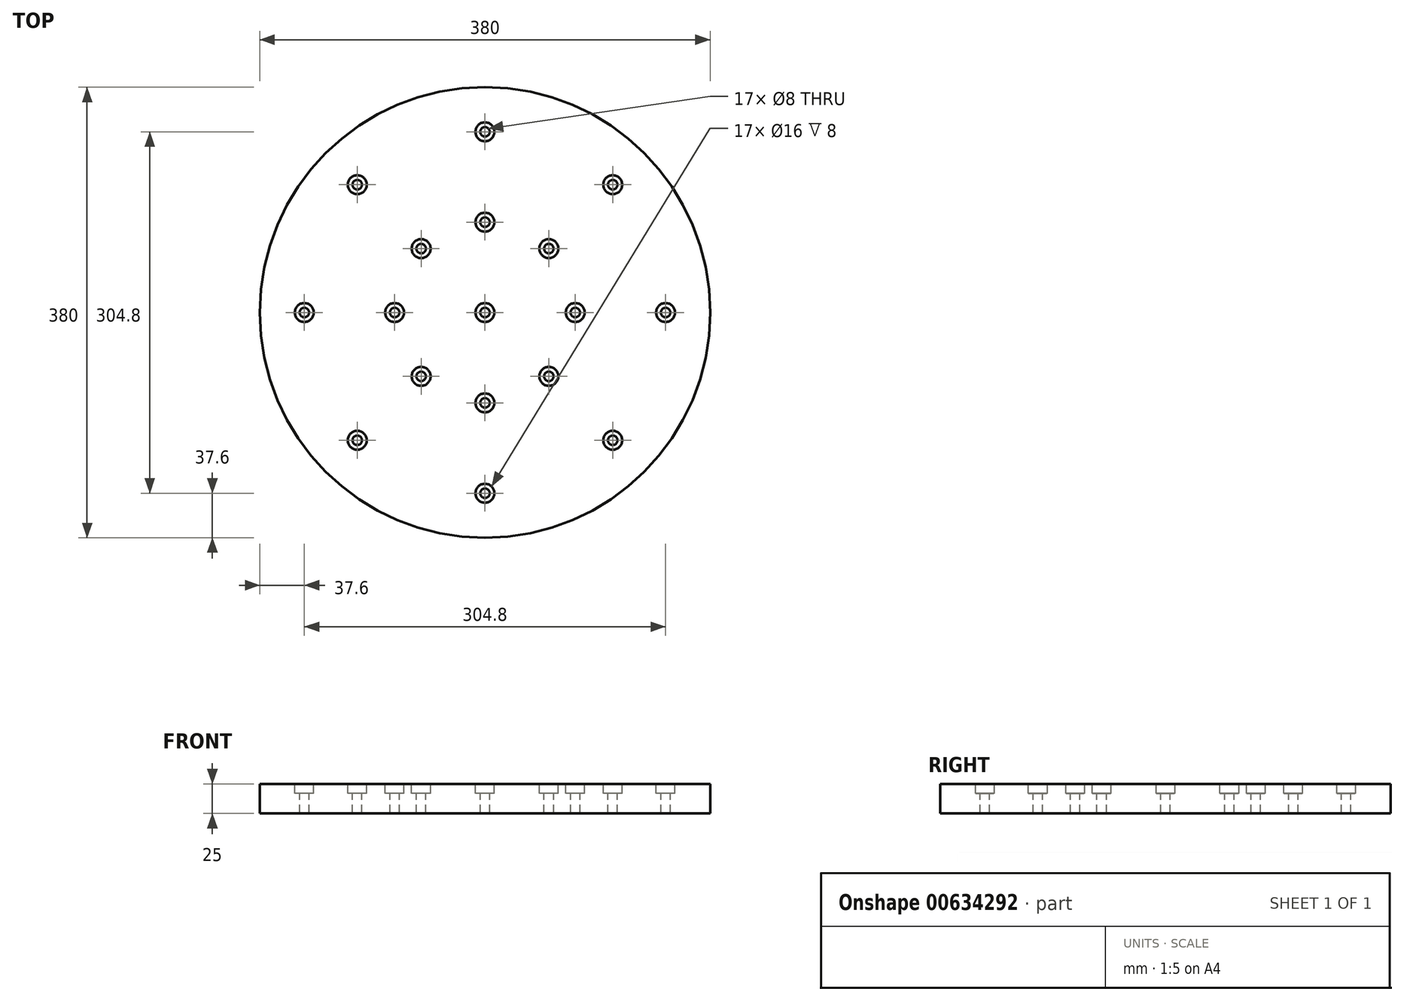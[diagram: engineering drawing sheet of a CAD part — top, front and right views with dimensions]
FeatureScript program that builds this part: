
annotation { "Feature Type Name" : "Feature", "Feature Type Description" : "" }
export const myFeature = defineFeature(function(context is Context, id is Id, definition is map)
    precondition{}
    {
        {
            var Q0;
            Q0=qCreatedBy(makeId("Top.planeOp"),FACE);
            var sketch = newSketch(context, id + "F0", { "sketchPlane" : qUnion([Q0])});
            skCircle(sketch, "E0", {"center": v(0, 0) * mm, "radius": 190 * mm});
            skSolve(sketch);
        }
        {
            var Q0;
            Q0 = qSketchRegion(id + "F0", true);
            extrude(context, id + "F1", {"entities" : qUnion([Q0]), "depth" : 25 * mm, "offsetDistance" : 25.4 * mm});
        }
        {
            var Q0;
            Q0=makeQuery(id+"F1.opExtrude","CAP_FACE",FACE,{"disambiguationData":[OSD([sQuery(id+"F0.wireOp",EDGE,"E0")])],"isStart":false});
            var sketch = newSketch(context, id + "F2", { "sketchPlane" : qUnion([Q0])});
            skCircle(sketch, "E1", {"center": v(0, 0) * mm, "radius": 76.2 * mm});
            skCircle(sketch, "E2", {"center": v(0, 0) * mm, "radius": 152.4 * mm});
            skCircle(sketch, "E3", {"center": v(0, 152.4) * mm, "radius": 4 * mm});
            skCircle(sketch, "E4", {"center": v(152.4, 0) * mm, "radius": 4 * mm});
            skCircle(sketch, "E5", {"center": v(0, -152.4) * mm, "radius": 4 * mm});
            skCircle(sketch, "E6", {"center": v(-152.4, 0) * mm, "radius": 4 * mm});
            skCircle(sketch, "E7", {"center": v(0, 76.2) * mm, "radius": 4 * mm});
            skCircle(sketch, "E8", {"center": v(76.2, 0) * mm, "radius": 4 * mm});
            skCircle(sketch, "E9", {"center": v(0, -76.2) * mm, "radius": 4 * mm});
            skCircle(sketch, "E10", {"center": v(-76.2, 0) * mm, "radius": 4 * mm});
            skLineSegment(sketch, "E11", {"start": v(0, -190) * mm, "end": v(0, 190) * mm});
            skLineSegment(sketch, "E12", {"start": v(190, 0) * mm, "end": v(-190, 0) * mm});
            skLineSegment(sketch, "E13", {"start": v(-134.35, -134.35) * mm, "end": v(0, 0) * mm});
            skLineSegment(sketch, "E14", {"start": v(0, 0) * mm, "end": v(134.35, 134.35) * mm});
            skLineSegment(sketch, "E15", {"start": v(0, 0) * mm, "end": v(134.35, -134.35) * mm});
            skLineSegment(sketch, "E16", {"start": v(0, 0) * mm, "end": v(-134.35, 134.35) * mm});
            skCircle(sketch, "E17", {"center": v(53.88, 53.88) * mm, "radius": 4 * mm});
            skCircle(sketch, "E18", {"center": v(53.88, -53.88) * mm, "radius": 4 * mm});
            skCircle(sketch, "E19", {"center": v(-53.88, -53.88) * mm, "radius": 4 * mm});
            skCircle(sketch, "E20", {"center": v(-53.88, 53.88) * mm, "radius": 4 * mm});
            skCircle(sketch, "E21", {"center": v(-107.76, 107.76) * mm, "radius": 4 * mm});
            skCircle(sketch, "E22", {"center": v(107.76, 107.76) * mm, "radius": 4 * mm});
            skCircle(sketch, "E23", {"center": v(107.76, -107.76) * mm, "radius": 4 * mm});
            skCircle(sketch, "E24", {"center": v(-107.76, -107.76) * mm, "radius": 4 * mm});
            skCircle(sketch, "E25", {"center": v(0, 152.4) * mm, "radius": 7 * mm});
            skCircle(sketch, "E26", {"center": v(0, 76.2) * mm, "radius": 7 * mm});
            skCircle(sketch, "E27", {"center": v(-107.76, 107.76) * mm, "radius": 7 * mm});
            skCircle(sketch, "E28", {"center": v(-53.88, 53.88) * mm, "radius": 7 * mm});
            skCircle(sketch, "E29", {"center": v(-152.4, 0) * mm, "radius": 7 * mm});
            skCircle(sketch, "E30", {"center": v(-76.2, 0) * mm, "radius": 7 * mm});
            skCircle(sketch, "E31", {"center": v(76.2, 0) * mm, "radius": 7 * mm});
            skCircle(sketch, "E32", {"center": v(152.4, 0) * mm, "radius": 7 * mm});
            skCircle(sketch, "E33", {"center": v(107.76, 107.76) * mm, "radius": 7 * mm});
            skCircle(sketch, "E34", {"center": v(107.76, -107.76) * mm, "radius": 7 * mm});
            skCircle(sketch, "E35", {"center": v(0, -76.2) * mm, "radius": 7 * mm});
            skCircle(sketch, "E36", {"center": v(0, -152.4) * mm, "radius": 7 * mm});
            skCircle(sketch, "E37", {"center": v(53.88, -53.88) * mm, "radius": 7 * mm});
            skCircle(sketch, "E38", {"center": v(53.88, 53.88) * mm, "radius": 7 * mm});
            skCircle(sketch, "E39", {"center": v(-53.88, -53.88) * mm, "radius": 7 * mm});
            skCircle(sketch, "E40", {"center": v(-107.76, -107.76) * mm, "radius": 7 * mm});
            skCircle(sketch, "E41", {"center": v(0, 0) * mm, "radius": 4 * mm});
            skCircle(sketch, "E42", {"center": v(0, 0) * mm, "radius": 7 * mm});
            skSolve(sketch);
        }
        {
            var Q0;
            Q0=sQuery(id+"F2.wireOp",VERTEX,"E29.center");
            var Q1;
            Q1=sQuery(id+"F2.wireOp",VERTEX,"E10.center");
            var Q2;
            Q2=sQuery(id+"F2.wireOp",VERTEX,"E1.center");
            var Q3;
            Q3=sQuery(id+"F2.wireOp",VERTEX,"E31.center");
            var Q4;
            Q4=sQuery(id+"F2.wireOp",VERTEX,"E4.center");
            var Q5;
            Q5=sQuery(id+"F2.wireOp",VERTEX,"E37.center");
            var Q6;
            Q6=sQuery(id+"F2.wireOp",VERTEX,"E34.center");
            var Q7;
            Q7=sQuery(id+"F2.wireOp",VERTEX,"E36.center");
            var Q8;
            Q8=sQuery(id+"F2.wireOp",VERTEX,"E35.center");
            var Q9;
            Q9=sQuery(id+"F2.wireOp",VERTEX,"E19.center");
            var Q10;
            Q10=sQuery(id+"F2.wireOp",VERTEX,"E24.center");
            var Q11;
            Q11=sQuery(id+"F2.wireOp",VERTEX,"E20.center");
            var Q12;
            Q12=sQuery(id+"F2.wireOp",VERTEX,"E17.center");
            var Q13;
            Q13=sQuery(id+"F2.wireOp",VERTEX,"E7.center");
            var Q14;
            Q14=sQuery(id+"F2.wireOp",VERTEX,"E33.center");
            var Q15;
            Q15=sQuery(id+"F2.wireOp",VERTEX,"E3.center");
            var Q16;
            Q16=sQuery(id+"F2.wireOp",VERTEX,"E21.center");
            var Q17;
            Q17=makeQuery(id+"F1.opExtrude","SWEPT_BODY",BODY,{"disambiguationData":[OSD([sQuery(id+"F0.wireOp",EDGE,"E0")])]});
            hole(context, id + "F3", {"style" : HoleStyle.C_BORE, "endStyle" : HoleEndStyle.THROUGH, "holeDiameter" : 8 * mm, "cBoreDiameter" : 16 * mm, "cBoreDepth" : 8 * mm, "majorDiameter" : 6.35 * mm, "isTappedThrough" : true, "tappedDepth" : 12.7 * mm, "tapClearance" : 3, "locations" : qUnion([Q0, Q1, Q2, Q3, Q4, Q5, Q6, Q7, Q8, Q9, Q10, Q11, Q12, Q13, Q14, Q15, Q16]), "scope" : qUnion([Q17])});
        }
    });
